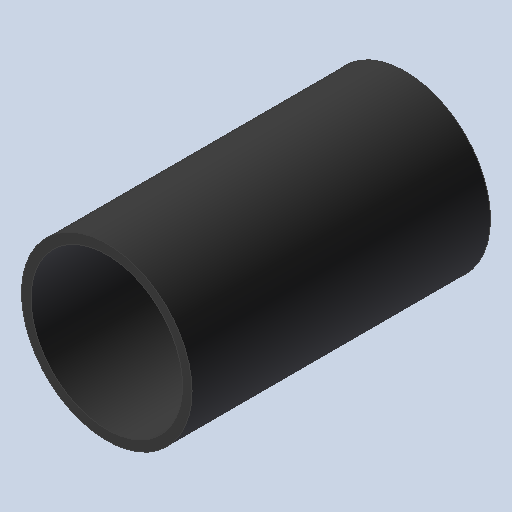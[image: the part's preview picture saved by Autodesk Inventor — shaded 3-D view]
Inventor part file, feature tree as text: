
AUTODESK INVENTOR PART (.ipt)
format: ipt  version: 2025.2 (Build 292293000, 293)  size: 99,328 bytes
history: native  units: in
note: dims shown in document units (in); Inventor stores cm internally (conversion verified against a paired STEP export)
features: other x3, sketch x1
ambient origin geometry x8: Origin, YZ Plane, XZ Plane, XY Plane, X Axis, Y Axis, Z Axis, Center Point
bodies: Solid1 (feature_tree)
feature tree (4):
  other  "TailBoomReinforcement.ipt"
  other  "Solid1::TailBoomReinforcement.ipt"
  other  "TaggingFeature1"
  sketch  "Sketch1"  dims[d0=0.3937in]
